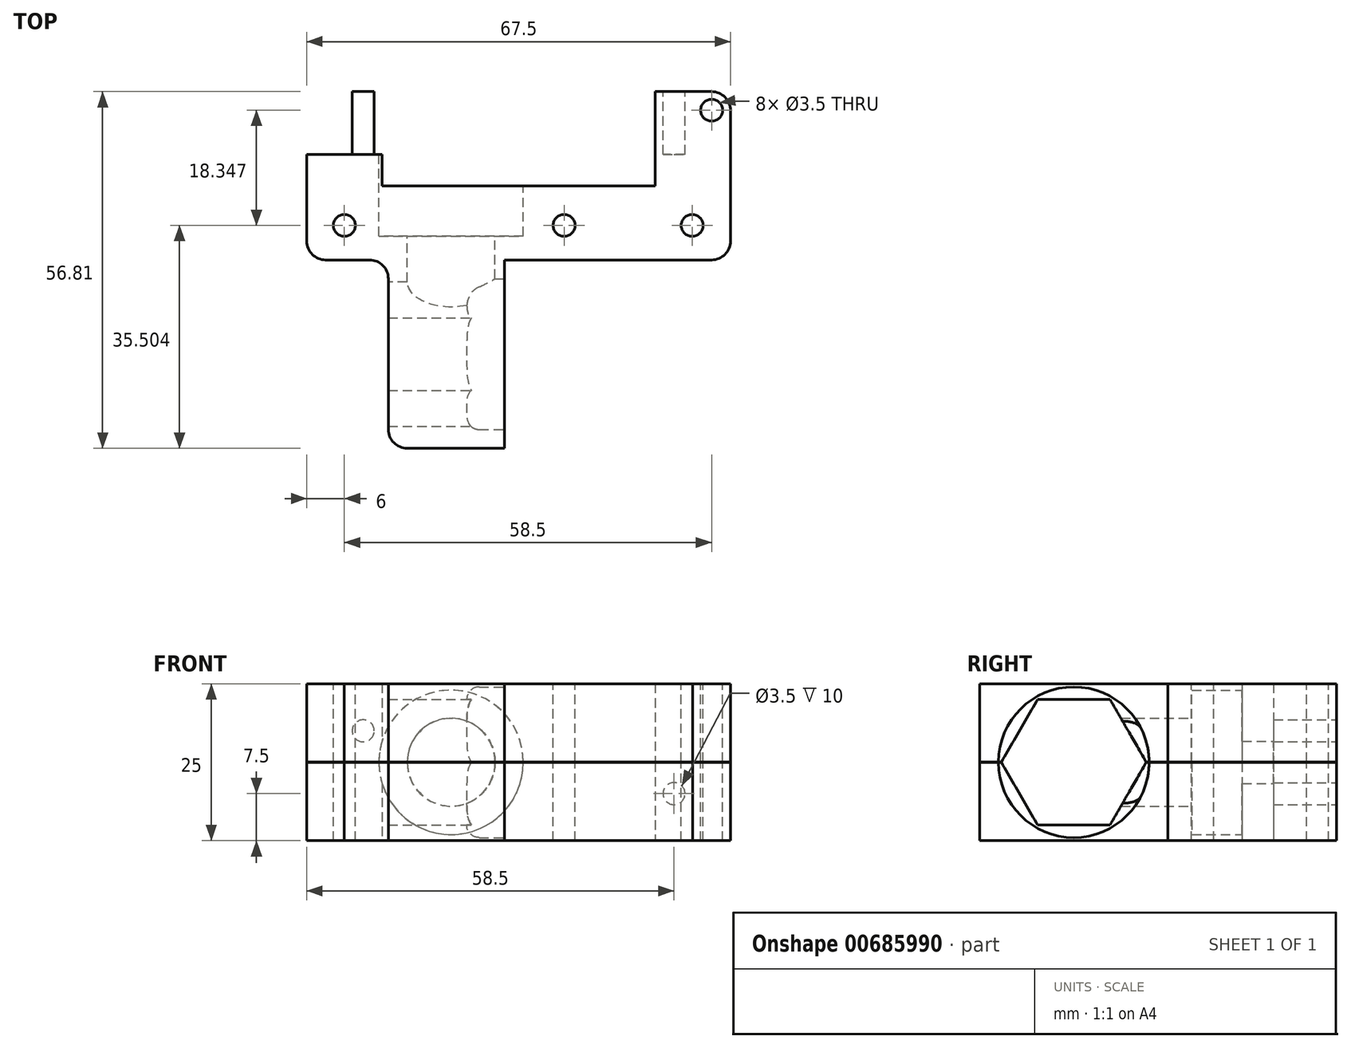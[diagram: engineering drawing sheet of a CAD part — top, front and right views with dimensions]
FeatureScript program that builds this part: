
annotation { "Feature Type Name" : "Feature", "Feature Type Description" : "" }
export const myFeature = defineFeature(function(context is Context, id is Id, definition is map)
    precondition{}
    {
        {
            var Q0;
            Q0=qCreatedBy(makeId("Top.planeOp"),FACE);
            var sketch = newSketch(context, id + "F0", { "sketchPlane" : qUnion([Q0])});
            skLineSegment(sketch, "E0.bottom", {"start": v(8.48, -15) * mm, "end": v(-10, -15) * mm});
            skLineSegment(sketch, "E0.top", {"start": v(10, 15) * mm, "end": v(-10, 15) * mm});
            skLineSegment(sketch, "E0.right", {"start": v(-10, -15) * mm, "end": v(-10, 15) * mm});
            skPoint(sketch, "E0.middle", {"position": v(0, 0) * mm});
            skPoint(sketch, "E1.middle", {"position": v(0, 29.32) * mm});
            skPoint(sketch, "E1.middle.positionSnap0", {"position": v(0, 15) * mm});
            skPoint(sketch, "E1.cornerSnap0", {"position": v(0, 15) * mm});
            skPoint(sketch, "E1.centerSnap0", {"position": v(0, 15) * mm});
            skLineSegment(sketch, "E2.bottom", {"start": v(17, 15) * mm, "end": v(-17, 15) * mm});
            skLineSegment(sketch, "E2.top", {"start": v(17, 26.81) * mm, "end": v(-17, 26.81) * mm});
            skLineSegment(sketch, "E2.right", {"start": v(-17, 15) * mm, "end": v(-17, 26.81) * mm});
            skPoint(sketch, "E2.middle", {"position": v(0, 20.9) * mm});
            skLineSegment(sketch, "E3.bottom", {"start": v(17, 26.81) * mm, "end": v(38.5, 26.81) * mm});
            skLineSegment(sketch, "E3.top", {"start": v(20, 15) * mm, "end": v(38.5, 15) * mm});
            skLineSegment(sketch, "E3.right", {"start": v(38.5, 26.81) * mm, "end": v(38.5, 15) * mm});
            skLineSegment(sketch, "E4", {"start": v(17, 15) * mm, "end": v(20, 15) * mm});
            skLineSegment(sketch, "E5.bottom", {"start": v(-10, -15) * mm, "end": v(-3, -15) * mm});
            skLineSegment(sketch, "E5.top", {"start": v(-10, -22) * mm, "end": v(-3, -22) * mm});
            skLineSegment(sketch, "E5.left", {"start": v(-10, -15) * mm, "end": v(-10, -22) * mm});
            skLineSegment(sketch, "E5.right", {"start": v(-3, -15) * mm, "end": v(-3, -22) * mm});
            skLineSegment(sketch, "E6.bottom", {"start": v(8.48, -15) * mm, "end": v(1.48, -15) * mm});
            skLineSegment(sketch, "E6.top", {"start": v(8.48, -22) * mm, "end": v(1.48, -22) * mm});
            skLineSegment(sketch, "E6.right", {"start": v(1.48, -15) * mm, "end": v(1.48, -22) * mm});
            skLineSegment(sketch, "E7", {"start": v(8.48, 15) * mm, "end": v(8.48, -22) * mm});
            skSolve(sketch);
        }
        {
            var Q0;
            Q0=makeQuery(id+"F0.imprint","IMPRINT",FACE,{"disambiguationData":[TD([[makeQuery(id+"F0.imprint","IMPRINT",EDGE,{"derivedFrom":sQuery(id+"F0.wireOp",EDGE,"E0.bottom")}),-1.0]])]});
            var Q1;
            Q1=makeQuery(id+"F0.imprint","IMPRINT",FACE,{"disambiguationData":[TD([[makeQuery(id+"F0.imprint","IMPRINT",EDGE,{"derivedFrom":sQuery(id+"F0.wireOp",EDGE,"E2.top")}),1.0]])]});
            var Q2;
            Q2=makeQuery(id+"F0.imprint","IMPRINT",FACE,{"disambiguationData":[TD([[makeQuery(id+"F0.imprint","IMPRINT",EDGE,{"derivedFrom":sQuery(id+"F0.wireOp",EDGE,"E5.bottom")}),-1.0]])]});
            var Q3;
            Q3=makeQuery(id+"F0.imprint","IMPRINT",FACE,{"disambiguationData":[TD([[makeQuery(id+"F0.imprint","IMPRINT",EDGE,{"derivedFrom":sQuery(id+"F0.wireOp",EDGE,"E6.bottom")}),1.0]])]});
            extrude(context, id + "F1", {"entities" : qUnion([Q0, Q1, Q2, Q3]), "depth" : 25 * mm, "offsetDistance" : 25 * mm});
        }
        {
            var Q0;
            Q0=makeQuery(id+"F1.opExtrude","SWEPT_FACE",FACE,{"disambiguationData":[OSD([sQuery(id+"F0.wireOp",EDGE,"E7")])]});
            var sketch = newSketch(context, id + "F2", { "sketchPlane" : qUnion([Q0])});
            skCircle(sketch, "E8.cCircle", {"center": v(0, 12.5) * mm, "radius": 10 * mm, "construction": true});
            skPoint(sketch, "E8.cCircle.centerSnap0", {"position": v(15, 12.5) * mm});
            skLineSegment(sketch, "E8.0", {"start": v(-5.77, 22.5) * mm, "end": v(5.77, 22.5) * mm});
            skLineSegment(sketch, "E8.1", {"start": v(5.77, 22.5) * mm, "end": v(11.55, 12.5) * mm});
            skLineSegment(sketch, "E8.2", {"start": v(11.55, 12.5) * mm, "end": v(5.77, 2.5) * mm});
            skLineSegment(sketch, "E8.3", {"start": v(5.77, 2.5) * mm, "end": v(-5.77, 2.5) * mm});
            skLineSegment(sketch, "E8.4", {"start": v(-5.77, 2.5) * mm, "end": v(-11.55, 12.5) * mm});
            skLineSegment(sketch, "E8.5", {"start": v(-11.55, 12.5) * mm, "end": v(-5.77, 22.5) * mm});
            skPoint(sketch, "E8.0.midPoint", {"position": v(0, 22.5) * mm});
            skCircle(sketch, "E9", {"center": v(0, 12.5) * mm, "radius": 12 * mm});
            skSolve(sketch);
        }
        {
            var Q0;
            {var subQ0=sQuery(id+"F2.wireOp",EDGE,"E9");var subQ5=sQuery(id+"F2.wireOp",EDGE,"E8.0");var subQ13=makeQuery(id+"F2.imprint","INTERSECT",VERTEX,{"disambiguationData":[OD(0.0)],"derivedFrom":[subQ5,subQ0]});Q0=makeQuery(id+"F2.imprint","IMPRINT",FACE,{"disambiguationData":[TD([[makeQuery(id+"F2.imprint","IMPRINT",EDGE,{"disambiguationData":[TD([[subQ13,-1.0]])],"derivedFrom":subQ5}),-1.0]])]});}
            var Q1;
            {var subQ0=sQuery(id+"F2.wireOp",EDGE,"E8.5");var subQ1=sQuery(id+"F2.wireOp",EDGE,"E8.4");var subQ2=makeQuery(id+"F2.imprint","INTERSECT",VERTEX,{"derivedFrom":[subQ1,subQ0]});Q1=makeQuery(id+"F2.imprint","IMPRINT",FACE,{"disambiguationData":[TD([[makeQuery(id+"F2.imprint","IMPRINT",EDGE,{"disambiguationData":[TD([[subQ2,1.0]])],"derivedFrom":subQ1}),-1.0]])]});}
            var Q2;
            {var subQ0=sQuery(id+"F2.wireOp",EDGE,"E8.5");var subQ1=sQuery(id+"F2.wireOp",EDGE,"E8.0");var subQ2=makeQuery(id+"F2.imprint","INTERSECT",VERTEX,{"derivedFrom":[subQ1,subQ0]});Q2=makeQuery(id+"F2.imprint","IMPRINT",FACE,{"disambiguationData":[TD([[makeQuery(id+"F2.imprint","IMPRINT",EDGE,{"disambiguationData":[TD([[subQ2,-1.0]])],"derivedFrom":subQ1}),-1.0]])]});}
            var Q3;
            {var subQ0=sQuery(id+"F2.wireOp",EDGE,"E8.1");var subQ1=sQuery(id+"F2.wireOp",EDGE,"E8.0");var subQ2=makeQuery(id+"F2.imprint","INTERSECT",VERTEX,{"derivedFrom":[subQ1,subQ0]});Q3=makeQuery(id+"F2.imprint","IMPRINT",FACE,{"disambiguationData":[TD([[makeQuery(id+"F2.imprint","IMPRINT",EDGE,{"disambiguationData":[TD([[subQ2,1.0]])],"derivedFrom":subQ1}),-1.0]])]});}
            var Q4;
            {var subQ0=sQuery(id+"F2.wireOp",EDGE,"E8.2");var subQ1=sQuery(id+"F2.wireOp",EDGE,"E8.1");var subQ2=makeQuery(id+"F2.imprint","INTERSECT",VERTEX,{"derivedFrom":[subQ1,subQ0]});Q4=makeQuery(id+"F2.imprint","IMPRINT",FACE,{"disambiguationData":[TD([[makeQuery(id+"F2.imprint","IMPRINT",EDGE,{"disambiguationData":[TD([[subQ2,1.0]])],"derivedFrom":subQ1}),-1.0]])]});}
            var Q5;
            {var subQ0=sQuery(id+"F2.wireOp",EDGE,"E8.3");var subQ1=sQuery(id+"F2.wireOp",EDGE,"E8.2");var subQ2=makeQuery(id+"F2.imprint","INTERSECT",VERTEX,{"derivedFrom":[subQ1,subQ0]});Q5=makeQuery(id+"F2.imprint","IMPRINT",FACE,{"disambiguationData":[TD([[makeQuery(id+"F2.imprint","IMPRINT",EDGE,{"disambiguationData":[TD([[subQ2,1.0]])],"derivedFrom":subQ1}),-1.0]])]});}
            var Q6;
            {var subQ0=sQuery(id+"F2.wireOp",EDGE,"E8.4");var subQ1=sQuery(id+"F2.wireOp",EDGE,"E8.3");var subQ2=makeQuery(id+"F2.imprint","INTERSECT",VERTEX,{"derivedFrom":[subQ1,subQ0]});Q6=makeQuery(id+"F2.imprint","IMPRINT",FACE,{"disambiguationData":[TD([[makeQuery(id+"F2.imprint","IMPRINT",EDGE,{"disambiguationData":[TD([[subQ2,1.0]])],"derivedFrom":subQ1}),-1.0]])]});}
            extrude(context, id + "F3", {"entities" : qUnion([Q0, Q1, Q2, Q3, Q4, Q5, Q6]), "operationType" : NewBodyOperationType.REMOVE, "oppositeDirection" : true, "depth" : 25 * mm, "offsetDistance" : 25 * mm});
        }
        {
            var Q0;
            {var subQ0=sQuery(id+"F2.wireOp",EDGE,"E9");var subQ1=sQuery(id+"F2.wireOp",EDGE,"E8.5");var subQ2=makeQuery(id+"F2.imprint","INTERSECT",VERTEX,{"disambiguationData":[OD(0.0)],"derivedFrom":[subQ1,subQ0]});Q0=makeQuery(id+"F2.imprint","IMPRINT",FACE,{"disambiguationData":[TD([[makeQuery(id+"F2.imprint","IMPRINT",EDGE,{"disambiguationData":[TD([[subQ2,-1.0]])],"derivedFrom":subQ1}),1.0]])]});}
            var Q1;
            {var subQ0=sQuery(id+"F2.wireOp",EDGE,"E9");var subQ1=sQuery(id+"F2.wireOp",EDGE,"E8.4");var subQ2=makeQuery(id+"F2.imprint","INTERSECT",VERTEX,{"disambiguationData":[OD(0.0)],"derivedFrom":[subQ1,subQ0]});Q1=makeQuery(id+"F2.imprint","IMPRINT",FACE,{"disambiguationData":[TD([[makeQuery(id+"F2.imprint","IMPRINT",EDGE,{"disambiguationData":[TD([[subQ2,-1.0]])],"derivedFrom":subQ1}),1.0]])]});}
            var Q2;
            {var subQ0=sQuery(id+"F2.wireOp",EDGE,"E9");var subQ1=sQuery(id+"F2.wireOp",EDGE,"E8.3");var subQ2=makeQuery(id+"F2.imprint","INTERSECT",VERTEX,{"disambiguationData":[OD(0.0)],"derivedFrom":[subQ1,subQ0]});Q2=makeQuery(id+"F2.imprint","IMPRINT",FACE,{"disambiguationData":[TD([[makeQuery(id+"F2.imprint","IMPRINT",EDGE,{"disambiguationData":[TD([[subQ2,-1.0]])],"derivedFrom":subQ1}),1.0]])]});}
            var Q3;
            {var subQ0=sQuery(id+"F2.wireOp",EDGE,"E9");var subQ1=sQuery(id+"F2.wireOp",EDGE,"E8.2");var subQ2=makeQuery(id+"F2.imprint","INTERSECT",VERTEX,{"disambiguationData":[OD(0.0)],"derivedFrom":[subQ1,subQ0]});Q3=makeQuery(id+"F2.imprint","IMPRINT",FACE,{"disambiguationData":[TD([[makeQuery(id+"F2.imprint","IMPRINT",EDGE,{"disambiguationData":[TD([[subQ2,-1.0]])],"derivedFrom":subQ1}),1.0]])]});}
            var Q4;
            {var subQ0=sQuery(id+"F2.wireOp",EDGE,"E9");var subQ1=sQuery(id+"F2.wireOp",EDGE,"E8.1");var subQ2=makeQuery(id+"F2.imprint","INTERSECT",VERTEX,{"disambiguationData":[OD(0.0)],"derivedFrom":[subQ1,subQ0]});Q4=makeQuery(id+"F2.imprint","IMPRINT",FACE,{"disambiguationData":[TD([[makeQuery(id+"F2.imprint","IMPRINT",EDGE,{"disambiguationData":[TD([[subQ2,-1.0]])],"derivedFrom":subQ1}),1.0]])]});}
            var Q5;
            {var subQ0=sQuery(id+"F2.wireOp",EDGE,"E9");var subQ1=sQuery(id+"F2.wireOp",EDGE,"E8.0");var subQ2=makeQuery(id+"F2.imprint","INTERSECT",VERTEX,{"disambiguationData":[OD(0.0)],"derivedFrom":[subQ1,subQ0]});Q5=makeQuery(id+"F2.imprint","IMPRINT",FACE,{"disambiguationData":[TD([[makeQuery(id+"F2.imprint","IMPRINT",EDGE,{"disambiguationData":[TD([[subQ2,-1.0]])],"derivedFrom":subQ1}),1.0]])]});}
            extrude(context, id + "F4", {"entities" : qUnion([Q0, Q1, Q2, Q3, Q4, Q5]), "operationType" : NewBodyOperationType.REMOVE, "oppositeDirection" : true, "depth" : 6 * mm, "offsetDistance" : 25 * mm});
        }
        {
            var Q0;
            Q0=makeQuery(id+"F1.opExtrude","SWEPT_FACE",FACE,{"disambiguationData":[OSD([sQuery(id+"F0.wireOp",EDGE,"E2.top")])]});
            var sketch = newSketch(context, id + "F5", { "sketchPlane" : qUnion([Q0])});
            skCircle(sketch, "E10", {"center": v(0, 12.5) * mm, "radius": 7 * mm});
            skPoint(sketch, "E10.centerSnap0", {"position": v(11.67, 12.5) * mm});
            skSolve(sketch);
        }
        {
            var Q0;
            Q0=makeQuery(id+"F5.imprint","IMPRINT",FACE,{"disambiguationData":[TD([[makeQuery(id+"F5.imprint","IMPRINT",EDGE,{"derivedFrom":sQuery(id+"F5.wireOp",EDGE,"E10")}),1.0]])]});
            extrude(context, id + "F6", {"entities" : qUnion([Q0]), "operationType" : NewBodyOperationType.REMOVE, "oppositeDirection" : true, "depth" : 20 * mm, "offsetDistance" : 25 * mm});
        }
        {
            var Q0;
            Q0=qCreatedBy(makeId("Top.planeOp"),FACE);
            var sketch = newSketch(context, id + "F7", { "sketchPlane" : qUnion([Q0])});
            skLineSegment(sketch, "E11.bottom", {"start": v(-17, 26.81) * mm, "end": v(-11, 26.81) * mm});
            skLineSegment(sketch, "E11.top", {"start": v(-17, 41.81) * mm, "end": v(-11, 41.81) * mm});
            skLineSegment(sketch, "E11.left", {"start": v(-17, 26.81) * mm, "end": v(-17, 41.81) * mm});
            skLineSegment(sketch, "E11.right", {"start": v(-11, 26.81) * mm, "end": v(-11, 41.81) * mm});
            skLineSegment(sketch, "E12.1.0.0", {"start": v(38.5, 26.81) * mm, "end": v(38.5, 41.81) * mm});
            skLineSegment(sketch, "E12.1.0.1", {"start": v(32.5, 26.81) * mm, "end": v(32.5, 41.81) * mm});
            skLineSegment(sketch, "E12.1.0.2", {"start": v(32.5, 41.81) * mm, "end": v(38.5, 41.81) * mm});
            skLineSegment(sketch, "E12.1.0.3", {"start": v(32.5, 26.81) * mm, "end": v(38.5, 26.81) * mm});
            skLineSegment(sketch, "E12.direction1", {"start": v(-17, 26.81) * mm, "end": v(32.5, 26.81) * mm, "construction": true});
            skLineSegment(sketch, "E13", {"start": v(-14, 41.81) * mm, "end": v(-14, 22.86) * mm, "construction": true});
            skLineSegment(sketch, "E14.bottom", {"start": v(-17, 41.81) * mm, "end": v(-23, 41.81) * mm});
            skLineSegment(sketch, "E14.top", {"start": v(-17, 15.01) * mm, "end": v(-23, 15.01) * mm});
            skLineSegment(sketch, "E14.left", {"start": v(-17, 41.81) * mm, "end": v(-17, 15.01) * mm});
            skLineSegment(sketch, "E14.right", {"start": v(-23, 41.81) * mm, "end": v(-23, 15.01) * mm});
            skLineSegment(sketch, "E15.bottom", {"start": v(38.5, 41.81) * mm, "end": v(44.5, 41.81) * mm});
            skLineSegment(sketch, "E15.top", {"start": v(38.5, 15.01) * mm, "end": v(44.5, 15.01) * mm});
            skLineSegment(sketch, "E15.left", {"start": v(38.5, 41.81) * mm, "end": v(38.5, 15.01) * mm});
            skLineSegment(sketch, "E15.right", {"start": v(44.5, 41.81) * mm, "end": v(44.5, 15.01) * mm});
            skSolve(sketch);
        }
        {
            var Q0;
            Q0=makeQuery(id+"F7.imprint","IMPRINT",FACE,{"disambiguationData":[TD([[makeQuery(id+"F7.imprint","IMPRINT",EDGE,{"derivedFrom":sQuery(id+"F7.wireOp",EDGE,"E11.bottom")}),1.0]])]});
            var Q1;
            Q1=makeQuery(id+"F7.imprint","IMPRINT",FACE,{"disambiguationData":[TD([[makeQuery(id+"F7.imprint","IMPRINT",EDGE,{"derivedFrom":sQuery(id+"F7.wireOp",EDGE,"E12.1.0.0")}),1.0]])]});
            var Q2;
            Q2=makeQuery(id+"F7.imprint","IMPRINT",FACE,{"disambiguationData":[TD([[makeQuery(id+"F7.imprint","IMPRINT",EDGE,{"derivedFrom":sQuery(id+"F7.wireOp",EDGE,"E14.bottom")}),1.0]])]});
            var Q3;
            Q3=makeQuery(id+"F7.imprint","IMPRINT",FACE,{"disambiguationData":[TD([[makeQuery(id+"F7.imprint","IMPRINT",EDGE,{"derivedFrom":sQuery(id+"F7.wireOp",EDGE,"E15.bottom")}),-1.0]])]});
            var Q4;
            Q4=makeQuery(id+"F7.imprint","IMPRINT",FACE,{"disambiguationData":[TD([[makeQuery(id+"F7.imprint","IMPRINT",EDGE,{"derivedFrom":sQuery(id+"F7.wireOp",EDGE,"E12.1.0.1")}),-1.0]])]});
            extrude(context, id + "F8", {"entities" : qUnion([Q0, Q1, Q2, Q3, Q4]), "operationType" : NewBodyOperationType.ADD, "depth" : 25 * mm, "offsetDistance" : 25 * mm});
        }
        {
            var Q0;
            Q0=makeQuery(id+"F8.opExtrude","SWEPT_FACE",FACE,{"disambiguationData":[OSD([sQuery(id+"F7.wireOp",EDGE,"E11.top")])]});
            var sketch = newSketch(context, id + "F9", { "sketchPlane" : qUnion([Q0])});
            skLineSegment(sketch, "E16", {"start": v(11, 12.5) * mm, "end": v(-40.93, 12.5) * mm, "construction": true});
            skCircle(sketch, "E17", {"center": v(14, 7.5) * mm, "radius": 1.75 * mm});
            skPoint(sketch, "E17.centerSnap0", {"position": v(17, 0) * mm});
            skCircle(sketch, "E18.MirrorC", {"center": v(14, 17.5) * mm, "radius": 1.75 * mm});
            skCircle(sketch, "E19.1.0.0", {"center": v(-35.5, 7.5) * mm, "radius": 1.75 * mm});
            skCircle(sketch, "E19.1.0.1", {"center": v(-35.5, 17.5) * mm, "radius": 1.75 * mm});
            skLineSegment(sketch, "E19.direction1", {"start": v(14, 7.5) * mm, "end": v(-35.5, 7.5) * mm, "construction": true});
            skSolve(sketch);
        }
        {
            var Q0;
            Q0=makeQuery(id+"F9.imprint","IMPRINT",FACE,{"disambiguationData":[TD([[makeQuery(id+"F9.imprint","IMPRINT",EDGE,{"derivedFrom":sQuery(id+"F9.wireOp",EDGE,"E17")}),1.0]])]});
            var Q1;
            Q1=makeQuery(id+"F9.imprint","IMPRINT",FACE,{"disambiguationData":[TD([[makeQuery(id+"F9.imprint","IMPRINT",EDGE,{"derivedFrom":sQuery(id+"F9.wireOp",EDGE,"E18.MirrorC")}),-1.0]])]});
            var Q2;
            Q2=makeQuery(id+"F9.imprint","IMPRINT",FACE,{"disambiguationData":[TD([[makeQuery(id+"F9.imprint","IMPRINT",EDGE,{"derivedFrom":sQuery(id+"F9.wireOp",EDGE,"E19.1.0.0")}),1.0]])]});
            var Q3;
            Q3=makeQuery(id+"F9.imprint","IMPRINT",FACE,{"disambiguationData":[TD([[makeQuery(id+"F9.imprint","IMPRINT",EDGE,{"derivedFrom":sQuery(id+"F9.wireOp",EDGE,"E19.1.0.1")}),-1.0]])]});
            extrude(context, id + "F10", {"entities" : qUnion([Q0, Q1, Q2, Q3]), "operationType" : NewBodyOperationType.REMOVE, "oppositeDirection" : true, "depth" : 10 * mm, "offsetDistance" : 25 * mm});
        }
        {
            var Q0;
            Q0=makeQuery(id+"F8.boolean.opBoolean","MERGE",FACE,{"derivedFrom":[makeQuery(id+"F1.opExtrude","CAP_FACE",FACE,{"disambiguationData":[OSD([sQuery(id+"F0.wireOp",EDGE,"E0.bottom"),sQuery(id+"F0.wireOp",EDGE,"E0.left"),sQuery(id+"F0.wireOp",EDGE,"E0.right"),sQuery(id+"F0.wireOp",EDGE,"E2.bottom"),sQuery(id+"F0.wireOp",EDGE,"E2.top"),sQuery(id+"F0.wireOp",EDGE,"E2.right"),sQuery(id+"F0.wireOp",EDGE,"E3.bottom"),sQuery(id+"F0.wireOp",EDGE,"E3.top"),sQuery(id+"F0.wireOp",EDGE,"E3.right"),sQuery(id+"F0.wireOp",EDGE,"E4"),sQuery(id+"F0.wireOp",EDGE,"E5.top"),sQuery(id+"F0.wireOp",EDGE,"E5.left"),sQuery(id+"F0.wireOp",EDGE,"E5.right"),sQuery(id+"F0.wireOp",EDGE,"E6.top"),sQuery(id+"F0.wireOp",EDGE,"E6.left"),sQuery(id+"F0.wireOp",EDGE,"E6.right")])],"isStart":false}),makeQuery(id+"F8.opExtrude","CAP_FACE",FACE,{"disambiguationData":[OSD([sQuery(id+"F7.wireOp",EDGE,"E11.bottom"),sQuery(id+"F7.wireOp",EDGE,"E11.top"),sQuery(id+"F7.wireOp",EDGE,"E11.right"),sQuery(id+"F7.wireOp",EDGE,"E14.bottom"),sQuery(id+"F7.wireOp",EDGE,"E14.top"),sQuery(id+"F7.wireOp",EDGE,"E14.left"),sQuery(id+"F7.wireOp",EDGE,"E14.right")])],"isStart":false}),makeQuery(id+"F8.opExtrude","CAP_FACE",FACE,{"disambiguationData":[OSD([sQuery(id+"F7.wireOp",EDGE,"E12.1.0.1"),sQuery(id+"F7.wireOp",EDGE,"E12.1.0.2"),sQuery(id+"F7.wireOp",EDGE,"E12.1.0.3"),sQuery(id+"F7.wireOp",EDGE,"E15.bottom"),sQuery(id+"F7.wireOp",EDGE,"E15.top"),sQuery(id+"F7.wireOp",EDGE,"E15.left"),sQuery(id+"F7.wireOp",EDGE,"E15.right")])],"isStart":false})]});
            var sketch = newSketch(context, id + "F11", { "sketchPlane" : qUnion([Q0])});
            skCircle(sketch, "E20", {"center": v(-6.5, -18.5) * mm, "radius": 1.8 * mm});
            skPoint(sketch, "E20.centerSnap0", {"position": v(-3, -18.5) * mm});
            skPoint(sketch, "E20.centerSnap1", {"position": v(-6.5, -22) * mm});
            skCircle(sketch, "E21.MirrorC", {"center": v(4.98, -18.5) * mm, "radius": 1.8 * mm});
            skCircle(sketch, "E22", {"center": v(-17, 20.5) * mm, "radius": 1.75 * mm});
            skCircle(sketch, "E23", {"center": v(38.4, 20.5) * mm, "radius": 1.75 * mm});
            skCircle(sketch, "E24", {"center": v(-20, 38.85) * mm, "radius": 1.75 * mm});
            skPoint(sketch, "E24.centerSnap0", {"position": v(-20, 15.01) * mm});
            skCircle(sketch, "E25", {"center": v(41.5, 38.85) * mm, "radius": 1.75 * mm});
            skPoint(sketch, "E25.centerSnap0", {"position": v(41.5, 15.01) * mm});
            skCircle(sketch, "E26.1.0.0", {"center": v(18, 20.5) * mm, "radius": 1.75 * mm});
            skLineSegment(sketch, "E26.direction1", {"start": v(-17, 20.5) * mm, "end": v(18, 20.5) * mm, "construction": true});
            skPoint(sketch, "E27", {"position": v(1.48, -18.5) * mm});
            skPoint(sketch, "E28", {"position": v(4.98, -22) * mm});
            skSolve(sketch);
        }
        {
            var Q0;
            Q0=makeQuery(id+"F11.imprint","IMPRINT",FACE,{"disambiguationData":[TD([[makeQuery(id+"F11.imprint","IMPRINT",EDGE,{"derivedFrom":sQuery(id+"F11.wireOp",EDGE,"E24")}),1.0]])]});
            var Q1;
            Q1=makeQuery(id+"F11.imprint","IMPRINT",FACE,{"disambiguationData":[TD([[makeQuery(id+"F11.imprint","IMPRINT",EDGE,{"derivedFrom":sQuery(id+"F11.wireOp",EDGE,"E22")}),1.0]])]});
            var Q2;
            Q2=makeQuery(id+"F11.imprint","IMPRINT",FACE,{"disambiguationData":[TD([[makeQuery(id+"F11.imprint","IMPRINT",EDGE,{"derivedFrom":sQuery(id+"F11.wireOp",EDGE,"E23")}),1.0]])]});
            var Q3;
            Q3=makeQuery(id+"F11.imprint","IMPRINT",FACE,{"disambiguationData":[TD([[makeQuery(id+"F11.imprint","IMPRINT",EDGE,{"derivedFrom":sQuery(id+"F11.wireOp",EDGE,"E25")}),1.0]])]});
            var Q4;
            Q4=makeQuery(id+"F11.imprint","IMPRINT",FACE,{"disambiguationData":[TD([[makeQuery(id+"F11.imprint","IMPRINT",EDGE,{"derivedFrom":sQuery(id+"F11.wireOp",EDGE,"E20")}),1.0]])]});
            var Q5;
            Q5=makeQuery(id+"F11.imprint","IMPRINT",FACE,{"disambiguationData":[TD([[makeQuery(id+"F11.imprint","IMPRINT",EDGE,{"derivedFrom":sQuery(id+"F11.wireOp",EDGE,"E21.MirrorC")}),-1.0]])]});
            var Q6;
            Q6=makeQuery(id+"F11.imprint","IMPRINT",FACE,{"disambiguationData":[TD([[makeQuery(id+"F11.imprint","IMPRINT",EDGE,{"derivedFrom":sQuery(id+"F11.wireOp",EDGE,"E26.1.0.0")}),1.0]])]});
            extrude(context, id + "F12", {"entities" : qUnion([Q0, Q1, Q2, Q3, Q4, Q5, Q6]), "operationType" : NewBodyOperationType.REMOVE, "oppositeDirection" : true, "depth" : 25 * mm, "offsetDistance" : 25 * mm});
        }
        {
            var Q0;
            Q0=makeQuery(id+"F5.imprint","IMPRINT",FACE,{"disambiguationData":[TD([[makeQuery(id+"F5.imprint","IMPRINT",EDGE,{"derivedFrom":sQuery(id+"F5.wireOp",EDGE,"E10")}),-1.0]])]});
            var sketch = newSketch(context, id + "F13", { "sketchPlane" : qUnion([Q0])});
            skCircle(sketch, "E29", {"center": v(0, 12.48) * mm, "radius": 11.5 * mm});
            skCircle(sketch, "E30", {"center": v(0, 12.48) * mm, "radius": 6.93 * mm});
            skSolve(sketch);
        }
        {
            var Q0;
            Q0=makeQuery(id+"F13.imprint","IMPRINT",FACE,{"disambiguationData":[TD([[makeQuery(id+"F13.imprint","IMPRINT",EDGE,{"derivedFrom":sQuery(id+"F13.wireOp",EDGE,"E29")}),1.0]])]});
            extrude(context, id + "F14", {"entities" : qUnion([Q0]), "operationType" : NewBodyOperationType.REMOVE, "oppositeDirection" : true, "depth" : 8 * mm, "offsetDistance" : 25 * mm, "hasSecondDirection" : true, "secondDirectionOppositeDirection" : false, "secondDirectionDepth" : 25 * mm});
        }
        {
            var Q0;
            Q0=makeQuery(id+"F1.opExtrude","SWEPT_EDGE",EDGE,{"disambiguationData":[OSD([sQuery(id+"F0.wireOp",EDGE,"E6.top"),sQuery(id+"F0.wireOp",EDGE,"E6.left")])]});
            var Q1;
            Q1=makeQuery(id+"F1.opExtrude","SWEPT_EDGE",EDGE,{"disambiguationData":[OSD([sQuery(id+"F0.wireOp",EDGE,"E6.top"),sQuery(id+"F0.wireOp",EDGE,"E6.right")])]});
            var Q2;
            Q2=makeQuery(id+"F1.opExtrude","SWEPT_EDGE",EDGE,{"disambiguationData":[OSD([sQuery(id+"F0.wireOp",EDGE,"E5.top"),sQuery(id+"F0.wireOp",EDGE,"E5.right")])]});
            var Q3;
            Q3=makeQuery(id+"F1.opExtrude","SWEPT_EDGE",EDGE,{"disambiguationData":[OSD([sQuery(id+"F0.wireOp",EDGE,"E5.top"),sQuery(id+"F0.wireOp",EDGE,"E5.left")])]});
            var Q4;
            Q4=makeQuery(id+"F8.opExtrude","SWEPT_EDGE",EDGE,{"disambiguationData":[OSD([sQuery(id+"F7.wireOp",EDGE,"E15.top"),sQuery(id+"F7.wireOp",EDGE,"E15.right")])]});
            var Q5;
            Q5=makeQuery(id+"F8.opExtrude","SWEPT_EDGE",EDGE,{"disambiguationData":[OSD([sQuery(id+"F7.wireOp",EDGE,"E15.bottom"),sQuery(id+"F7.wireOp",EDGE,"E15.right")])]});
            var Q6;
            Q6=makeQuery(id+"F8.opExtrude","SWEPT_EDGE",EDGE,{"disambiguationData":[OSD([sQuery(id+"F7.wireOp",EDGE,"E14.top"),sQuery(id+"F7.wireOp",EDGE,"E14.right")])]});
            var Q7;
            Q7=makeQuery(id+"F1.opExtrude","SWEPT_EDGE",EDGE,{"disambiguationData":[OSD([sQuery(id+"F0.wireOp",EDGE,"E0.left"),sQuery(id+"F0.wireOp",EDGE,"E2.bottom")])]});
            var Q8;
            Q8=makeQuery(id+"F1.opExtrude","SWEPT_EDGE",EDGE,{"disambiguationData":[OSD([sQuery(id+"F0.wireOp",EDGE,"E0.right"),sQuery(id+"F0.wireOp",EDGE,"E2.bottom")])]});
            var Q9;
            Q9=makeQuery(id+"F8.opExtrude","SWEPT_EDGE",EDGE,{"disambiguationData":[OSD([sQuery(id+"F7.wireOp",EDGE,"E14.bottom"),sQuery(id+"F7.wireOp",EDGE,"E14.right")])]});
            var Q10;
            Q10=makeQuery(id+"F8.opExtrude","SWEPT_EDGE",EDGE,{"disambiguationData":[OSD([sQuery(id+"F7.wireOp",EDGE,"E12.1.0.1"),sQuery(id+"F7.wireOp",EDGE,"E12.1.0.3")])]});
            fillet(context, id + "F15", {"entities" : qUnion([Q0, Q1, Q2, Q3, Q4, Q5, Q6, Q7, Q8, Q9, Q10]), "radius" : 3 * mm, "tangentPropagation" : true, "allowEdgeOverflow" : false});
        }
        {
            var Q0;
            Q0=makeQuery(id+"F8.opExtrude","SWEPT_FACE",FACE,{"disambiguationData":[OSD([sQuery(id+"F7.wireOp",EDGE,"E15.right")])]});
            var sketch = newSketch(context, id + "F16", { "sketchPlane" : qUnion([Q0])});
            skLineSegment(sketch, "E31.bottom", {"start": v(62.83, 12.45) * mm, "end": v(-26.8, 12.45) * mm});
            skLineSegment(sketch, "E31.top", {"start": v(62.83, 12.55) * mm, "end": v(-26.8, 12.55) * mm});
            skLineSegment(sketch, "E31.left", {"start": v(62.83, 12.45) * mm, "end": v(62.83, 12.55) * mm});
            skLineSegment(sketch, "E31.right", {"start": v(-26.8, 12.45) * mm, "end": v(-26.8, 12.55) * mm});
            skPoint(sketch, "E31.middle", {"position": v(18.01, 12.5) * mm});
            skSolve(sketch);
        }
        {
            var Q0;
            {var subQ0=sQuery(id+"F16.wireOp",EDGE,"E31.left");Q0=makeQuery(id+"F16.imprint","IMPRINT",FACE,{"disambiguationData":[TD([[makeQuery(id+"F16.imprint","IMPRINT",EDGE,{"derivedFrom":subQ0}),1.0]])]});}
            var Q1;
            {var subQ0=sQuery(id+"F16.wireOp",EDGE,"E31.bottom");var subQ1=sQuery(id+"F7.wireOp",EDGE,"E15.right");var subQ2=makeQuery(id+"F8.opExtrude","SWEPT_FACE",FACE,{"disambiguationData":[OSD([subQ1])]});var subQ3=makeQuery(id+"F15.opFillet","BLEND_EDGE",EDGE,{"blendedFrom":[makeQuery(id+"F8.opExtrude","SWEPT_EDGE",EDGE,{"disambiguationData":[OSD([sQuery(id+"F7.wireOp",EDGE,"E15.bottom"),subQ1])]}),subQ2],"blendedInto":[subQ2]});var subQ4=makeQuery(id+"F16.imprint","INTERSECT",VERTEX,{"derivedFrom":[subQ3,subQ0]});Q1=makeQuery(id+"F16.imprint","IMPRINT",FACE,{"disambiguationData":[TD([[makeQuery(id+"F16.imprint","IMPRINT",EDGE,{"disambiguationData":[TD([[subQ4,-1.0]])],"derivedFrom":subQ0}),-1.0]])]});}
            var Q2;
            {var subQ0=sQuery(id+"F16.wireOp",EDGE,"E31.right");Q2=makeQuery(id+"F16.imprint","IMPRINT",FACE,{"disambiguationData":[TD([[makeQuery(id+"F16.imprint","IMPRINT",EDGE,{"derivedFrom":subQ0}),-1.0]])]});}
            extrude(context, id + "F17", {"entities" : qUnion([Q0, Q1, Q2]), "operationType" : NewBodyOperationType.REMOVE, "oppositeDirection" : true, "depth" : 150 * mm, "offsetDistance" : 25 * mm});
        }
        {
            var Q0;
            {var subQ0=sQuery(id+"F2.wireOp",EDGE,"E9");Q0=makeQuery(id+"F17.boolean.opBoolean","SPLIT",EDGE,{"disambiguationData":[TD([makeQuery(id+"F17.opExtrude","SWEPT_FACE",FACE,{"disambiguationData":[OSD([sQuery(id+"F16.wireOp",EDGE,"E31.bottom")])]})])],"derivedFrom":makeQuery(id+"F4.boolean.opBoolean","COPY",EDGE,{"derivedFrom":makeQuery(id+"F4.opExtrude","CAP_EDGE",EDGE,{"disambiguationData":[OSD([subQ0])],"isStart":false})})});}
            var Q1;
            {var subQ0=sQuery(id+"F2.wireOp",EDGE,"E9");Q1=makeQuery(id+"F17.boolean.opBoolean","SPLIT",EDGE,{"disambiguationData":[TD([makeQuery(id+"F17.opExtrude","SWEPT_FACE",FACE,{"disambiguationData":[OSD([sQuery(id+"F16.wireOp",EDGE,"E31.top")])]})])],"derivedFrom":makeQuery(id+"F4.boolean.opBoolean","COPY",EDGE,{"derivedFrom":makeQuery(id+"F4.opExtrude","CAP_EDGE",EDGE,{"disambiguationData":[OSD([subQ0])],"isStart":false})})});}
            fillet(context, id + "F18", {"entities" : qUnion([Q0, Q1]), "radius" : 2 * mm, "tangentPropagation" : true, "allowEdgeOverflow" : false});
        }
    });
